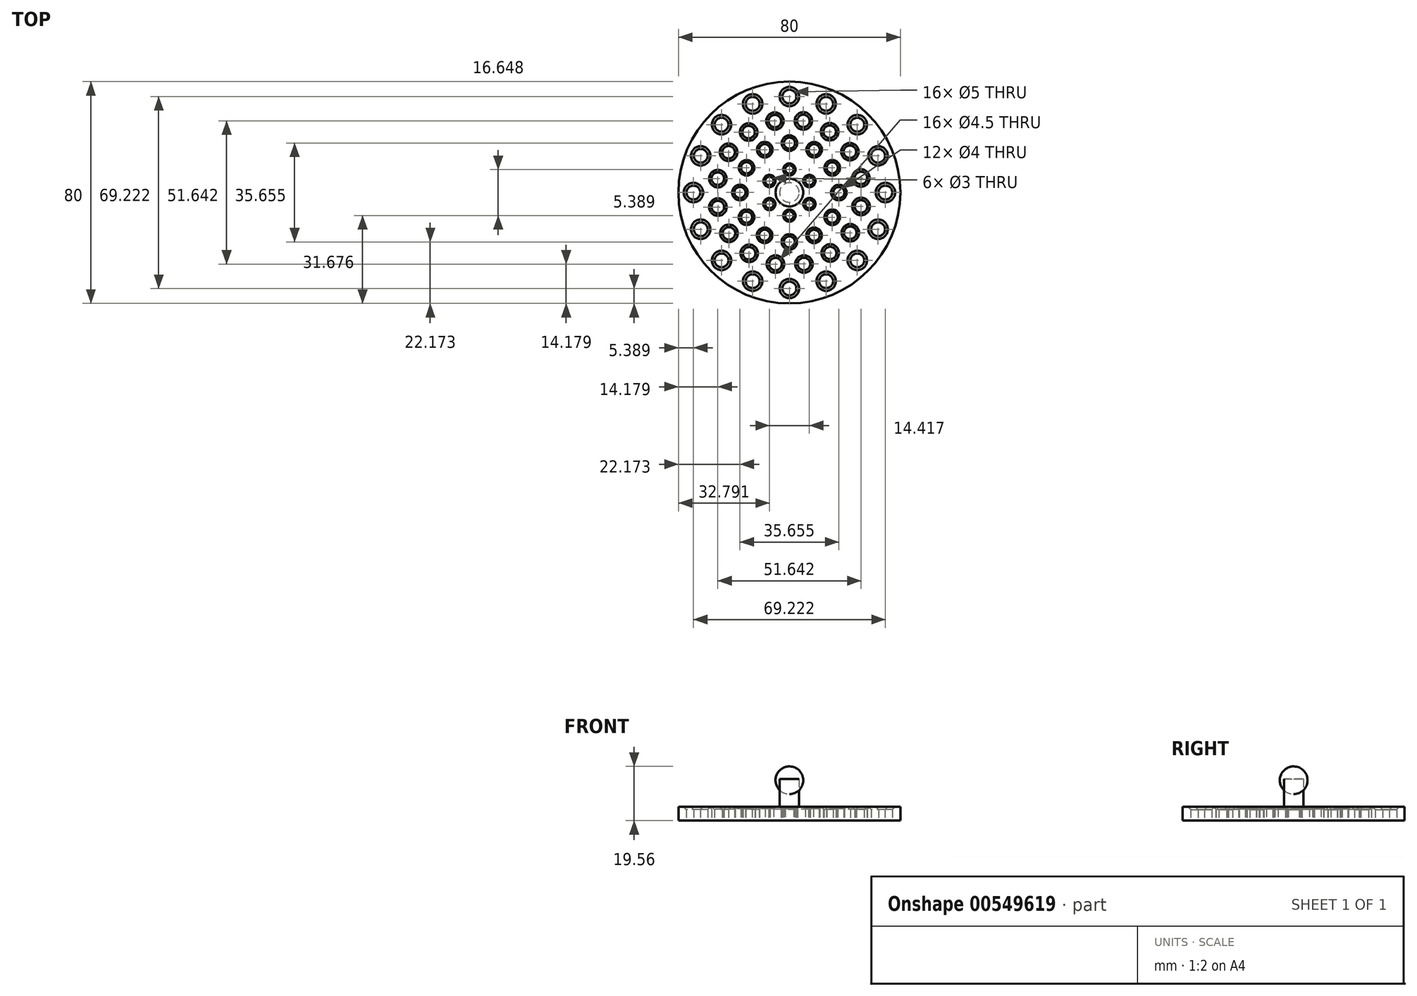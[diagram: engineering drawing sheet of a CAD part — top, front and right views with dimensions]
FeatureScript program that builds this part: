
annotation { "Feature Type Name" : "Feature", "Feature Type Description" : "" }
export const myFeature = defineFeature(function(context is Context, id is Id, definition is map)
    precondition{}
    {
        {
            var Q0;
            Q0=qCreatedBy(makeId("Top.planeOp"),FACE);
            var sketch = newSketch(context, id + "F0", { "sketchPlane" : qUnion([Q0])});
            skCircle(sketch, "E0", {"center": v(0, 0) * mm, "radius": 40 * mm});
            skCircle(sketch, "E1", {"center": v(0, 0) * mm, "radius": 3.5 * mm});
            skCircle(sketch, "E2", {"center": v(0, -34.61) * mm, "radius": 2.5 * mm});
            skCircle(sketch, "E3.1.0", {"center": v(13.25, -31.98) * mm, "radius": 2.5 * mm});
            skCircle(sketch, "E3.2.0", {"center": v(24.47, -24.47) * mm, "radius": 2.5 * mm});
            skCircle(sketch, "E4.1.3.0", {"center": v(31.98, -13.25) * mm, "radius": 2.5 * mm});
            skCircle(sketch, "E4.1.4.0", {"center": v(34.61, 0) * mm, "radius": 2.5 * mm});
            skCircle(sketch, "E4.1.5.0", {"center": v(31.98, 13.25) * mm, "radius": 2.5 * mm});
            skCircle(sketch, "E4.1.6.0", {"center": v(24.47, 24.47) * mm, "radius": 2.5 * mm});
            skCircle(sketch, "E4.1.7.0", {"center": v(13.25, 31.98) * mm, "radius": 2.5 * mm});
            skCircle(sketch, "E4.1.8.0", {"center": v(0, 34.61) * mm, "radius": 2.5 * mm});
            skCircle(sketch, "E4.1.9.0", {"center": v(-13.25, 31.98) * mm, "radius": 2.5 * mm});
            skCircle(sketch, "E5.1.10.0", {"center": v(-24.47, 24.47) * mm, "radius": 2.5 * mm});
            skCircle(sketch, "E5.1.11.0", {"center": v(-31.98, 13.25) * mm, "radius": 2.5 * mm});
            skCircle(sketch, "E6", {"center": v(-0.02, -17.83) * mm, "radius": 2 * mm});
            skCircle(sketch, "E7.1.0", {"center": v(8.9, -15.45) * mm, "radius": 2 * mm});
            skCircle(sketch, "E7.2.0", {"center": v(15.43, -8.93) * mm, "radius": 2 * mm});
            skCircle(sketch, "E8.1.3.0", {"center": v(17.83, -0.02) * mm, "radius": 2 * mm});
            skCircle(sketch, "E8.1.4.0", {"center": v(15.45, 8.9) * mm, "radius": 2 * mm});
            skCircle(sketch, "E8.1.5.0", {"center": v(8.93, 15.43) * mm, "radius": 2 * mm});
            skCircle(sketch, "E8.1.6.0", {"center": v(0.02, 17.83) * mm, "radius": 2 * mm});
            skCircle(sketch, "E8.1.7.0", {"center": v(-8.9, 15.45) * mm, "radius": 2 * mm});
            skCircle(sketch, "E9.1.8.0", {"center": v(-15.43, 8.93) * mm, "radius": 2 * mm});
            skCircle(sketch, "E9.1.9.0", {"center": v(-17.83, 0.02) * mm, "radius": 2 * mm});
            skCircle(sketch, "E10.1.12.0", {"center": v(-34.61, 0) * mm, "radius": 2.5 * mm});
            skCircle(sketch, "E10.1.13.0", {"center": v(-31.98, -13.25) * mm, "radius": 2.5 * mm});
            skCircle(sketch, "E11.1.10.0", {"center": v(-15.45, -8.9) * mm, "radius": 2 * mm});
            skCircle(sketch, "E11.1.11.0", {"center": v(-8.93, -15.43) * mm, "radius": 2 * mm});
            skCircle(sketch, "E12.1.14.0", {"center": v(-24.47, -24.47) * mm, "radius": 2.5 * mm});
            skCircle(sketch, "E12.1.15.0", {"center": v(-13.25, -31.98) * mm, "radius": 2.5 * mm});
            skCircle(sketch, "E13.2.0", {"center": v(-5.02, -25.82) * mm, "radius": 2.25 * mm});
            skCircle(sketch, "E14.1.0", {"center": v(5.24, -25.78) * mm, "radius": 2.25 * mm});
            skCircle(sketch, "E14.2.0", {"center": v(14.7, -21.8) * mm, "radius": 2.25 * mm});
            skCircle(sketch, "E14.3.0", {"center": v(21.93, -14.52) * mm, "radius": 2.25 * mm});
            skCircle(sketch, "E14.4.0", {"center": v(25.82, -5.02) * mm, "radius": 2.25 * mm});
            skCircle(sketch, "E14.5.0", {"center": v(25.78, 5.24) * mm, "radius": 2.25 * mm});
            skCircle(sketch, "E14.6.0", {"center": v(21.8, 14.7) * mm, "radius": 2.25 * mm});
            skCircle(sketch, "E14.7.0", {"center": v(14.52, 21.93) * mm, "radius": 2.25 * mm});
            skCircle(sketch, "E14.8.0", {"center": v(5.02, 25.82) * mm, "radius": 2.25 * mm});
            skCircle(sketch, "E14.9.0", {"center": v(-5.24, 25.78) * mm, "radius": 2.25 * mm});
            skCircle(sketch, "E14.10.0", {"center": v(-14.7, 21.8) * mm, "radius": 2.25 * mm});
            skCircle(sketch, "E14.11.0", {"center": v(-21.93, 14.52) * mm, "radius": 2.25 * mm});
            skCircle(sketch, "E14.12.0", {"center": v(-25.82, 5.02) * mm, "radius": 2.25 * mm});
            skCircle(sketch, "E14.13.0", {"center": v(-25.78, -5.24) * mm, "radius": 2.25 * mm});
            skCircle(sketch, "E14.14.0", {"center": v(-21.8, -14.7) * mm, "radius": 2.25 * mm});
            skCircle(sketch, "E14.15.0", {"center": v(-14.52, -21.93) * mm, "radius": 2.25 * mm});
            skCircle(sketch, "E15", {"center": v(0, -8.32) * mm, "radius": 1.5 * mm});
            skCircle(sketch, "E16.1.0", {"center": v(7.2, -4.16) * mm, "radius": 1.5 * mm});
            skCircle(sketch, "E16.2.0", {"center": v(7.2, 4.16) * mm, "radius": 1.5 * mm});
            skCircle(sketch, "E16.3.0", {"center": v(0, 8.32) * mm, "radius": 1.5 * mm});
            skCircle(sketch, "E17.1.4.0", {"center": v(-7.2, 4.16) * mm, "radius": 1.5 * mm});
            skCircle(sketch, "E17.1.5.0", {"center": v(-7.2, -4.16) * mm, "radius": 1.5 * mm});
            skSolve(sketch);
        }
        {
            var Q0;
            Q0=makeQuery(id+"F0.imprint","IMPRINT",FACE,{"disambiguationData":[TD([[makeQuery(id+"F0.imprint","IMPRINT",EDGE,{"derivedFrom":sQuery(id+"F0.wireOp",EDGE,"E0")}),1.0]])]});
            var Q1;
            Q1=sQuery(id+"F0.wireOp",EDGE,"E0");
            extrude(context, id + "F1", {"entities" : qUnion([Q0]), "surfaceEntities" : qUnion([Q1]), "depth" : 5 * mm, "offsetDistance" : 25 * mm});
        }
        {
            var Q0;
            Q0=makeQuery(id+"F0.imprint","IMPRINT",FACE,{"disambiguationData":[TD([[makeQuery(id+"F0.imprint","IMPRINT",EDGE,{"derivedFrom":sQuery(id+"F0.wireOp",EDGE,"E1")}),1.0]])]});
            var Q1;
            Q1=sQuery(id+"F0.wireOp",EDGE,"E1");
            extrude(context, id + "F2", {"entities" : qUnion([Q0]), "operationType" : NewBodyOperationType.ADD, "surfaceEntities" : qUnion([Q1]), "depth" : 15 * mm, "offsetDistance" : 25 * mm});
        }
        {
            var Q0;
            Q0=makeQuery(id+"F1.opExtrude","CAP_EDGE",EDGE,{"disambiguationData":[OSD([sQuery(id+"F0.wireOp",EDGE,"E10.1.12.0")])],"isStart":false});
            var Q1;
            Q1=makeQuery(id+"F1.opExtrude","CAP_EDGE",EDGE,{"disambiguationData":[OSD([sQuery(id+"F0.wireOp",EDGE,"E5.1.11.0")])],"isStart":false});
            var Q2;
            Q2=makeQuery(id+"F1.opExtrude","CAP_EDGE",EDGE,{"disambiguationData":[OSD([sQuery(id+"F0.wireOp",EDGE,"E5.1.10.0")])],"isStart":false});
            var Q3;
            Q3=makeQuery(id+"F1.opExtrude","CAP_EDGE",EDGE,{"disambiguationData":[OSD([sQuery(id+"F0.wireOp",EDGE,"E4.1.9.0")])],"isStart":false});
            var Q4;
            Q4=makeQuery(id+"F1.opExtrude","CAP_EDGE",EDGE,{"disambiguationData":[OSD([sQuery(id+"F0.wireOp",EDGE,"E4.1.8.0")])],"isStart":false});
            var Q5;
            Q5=makeQuery(id+"F1.opExtrude","CAP_EDGE",EDGE,{"disambiguationData":[OSD([sQuery(id+"F0.wireOp",EDGE,"E4.1.7.0")])],"isStart":false});
            var Q6;
            Q6=makeQuery(id+"F1.opExtrude","CAP_EDGE",EDGE,{"disambiguationData":[OSD([sQuery(id+"F0.wireOp",EDGE,"E4.1.6.0")])],"isStart":false});
            var Q7;
            Q7=makeQuery(id+"F1.opExtrude","CAP_EDGE",EDGE,{"disambiguationData":[OSD([sQuery(id+"F0.wireOp",EDGE,"E4.1.5.0")])],"isStart":false});
            var Q8;
            Q8=makeQuery(id+"F1.opExtrude","CAP_EDGE",EDGE,{"disambiguationData":[OSD([sQuery(id+"F0.wireOp",EDGE,"E4.1.4.0")])],"isStart":false});
            var Q9;
            Q9=makeQuery(id+"F1.opExtrude","CAP_EDGE",EDGE,{"disambiguationData":[OSD([sQuery(id+"F0.wireOp",EDGE,"E4.1.3.0")])],"isStart":false});
            var Q10;
            Q10=makeQuery(id+"F1.opExtrude","CAP_EDGE",EDGE,{"disambiguationData":[OSD([sQuery(id+"F0.wireOp",EDGE,"E3.2.0")])],"isStart":false});
            var Q11;
            Q11=makeQuery(id+"F1.opExtrude","CAP_EDGE",EDGE,{"disambiguationData":[OSD([sQuery(id+"F0.wireOp",EDGE,"E3.1.0")])],"isStart":false});
            var Q12;
            Q12=makeQuery(id+"F1.opExtrude","CAP_EDGE",EDGE,{"disambiguationData":[OSD([sQuery(id+"F0.wireOp",EDGE,"E2")])],"isStart":false});
            var Q13;
            Q13=makeQuery(id+"F1.opExtrude","CAP_EDGE",EDGE,{"disambiguationData":[OSD([sQuery(id+"F0.wireOp",EDGE,"E12.1.15.0")])],"isStart":false});
            var Q14;
            Q14=makeQuery(id+"F1.opExtrude","CAP_EDGE",EDGE,{"disambiguationData":[OSD([sQuery(id+"F0.wireOp",EDGE,"E12.1.14.0")])],"isStart":false});
            var Q15;
            Q15=makeQuery(id+"F1.opExtrude","CAP_EDGE",EDGE,{"disambiguationData":[OSD([sQuery(id+"F0.wireOp",EDGE,"E10.1.13.0")])],"isStart":false});
            chamfer(context, id + "F3", {"entities" : qUnion([Q0, Q1, Q2, Q3, Q4, Q5, Q6, Q7, Q8, Q9, Q10, Q11, Q12, Q13, Q14, Q15]), "width" : 1 * mm, "tangentPropagation" : true});
        }
        {
            var Q0;
            Q0=makeQuery(id+"F1.opExtrude","CAP_EDGE",EDGE,{"disambiguationData":[OSD([sQuery(id+"F0.wireOp",EDGE,"E14.11.0")])],"isStart":false});
            var Q1;
            Q1=makeQuery(id+"F1.opExtrude","CAP_EDGE",EDGE,{"disambiguationData":[OSD([sQuery(id+"F0.wireOp",EDGE,"E14.10.0")])],"isStart":false});
            var Q2;
            Q2=makeQuery(id+"F1.opExtrude","CAP_EDGE",EDGE,{"disambiguationData":[OSD([sQuery(id+"F0.wireOp",EDGE,"E14.8.0")])],"isStart":false});
            var Q3;
            Q3=makeQuery(id+"F1.opExtrude","CAP_EDGE",EDGE,{"disambiguationData":[OSD([sQuery(id+"F0.wireOp",EDGE,"E14.7.0")])],"isStart":false});
            var Q4;
            Q4=makeQuery(id+"F1.opExtrude","CAP_EDGE",EDGE,{"disambiguationData":[OSD([sQuery(id+"F0.wireOp",EDGE,"E14.6.0")])],"isStart":false});
            var Q5;
            Q5=makeQuery(id+"F1.opExtrude","CAP_EDGE",EDGE,{"disambiguationData":[OSD([sQuery(id+"F0.wireOp",EDGE,"E14.5.0")])],"isStart":false});
            var Q6;
            Q6=makeQuery(id+"F1.opExtrude","CAP_EDGE",EDGE,{"disambiguationData":[OSD([sQuery(id+"F0.wireOp",EDGE,"E14.4.0")])],"isStart":false});
            var Q7;
            Q7=makeQuery(id+"F1.opExtrude","CAP_EDGE",EDGE,{"disambiguationData":[OSD([sQuery(id+"F0.wireOp",EDGE,"E14.3.0")])],"isStart":false});
            var Q8;
            Q8=makeQuery(id+"F1.opExtrude","CAP_EDGE",EDGE,{"disambiguationData":[OSD([sQuery(id+"F0.wireOp",EDGE,"E14.2.0")])],"isStart":false});
            var Q9;
            Q9=makeQuery(id+"F1.opExtrude","CAP_EDGE",EDGE,{"disambiguationData":[OSD([sQuery(id+"F0.wireOp",EDGE,"E14.1.0")])],"isStart":false});
            var Q10;
            Q10=makeQuery(id+"F1.opExtrude","CAP_EDGE",EDGE,{"disambiguationData":[OSD([sQuery(id+"F0.wireOp",EDGE,"E13.2.0")])],"isStart":false});
            var Q11;
            Q11=makeQuery(id+"F1.opExtrude","CAP_EDGE",EDGE,{"disambiguationData":[OSD([sQuery(id+"F0.wireOp",EDGE,"E14.15.0")])],"isStart":false});
            var Q12;
            Q12=makeQuery(id+"F1.opExtrude","CAP_EDGE",EDGE,{"disambiguationData":[OSD([sQuery(id+"F0.wireOp",EDGE,"E14.14.0")])],"isStart":false});
            var Q13;
            Q13=makeQuery(id+"F1.opExtrude","CAP_EDGE",EDGE,{"disambiguationData":[OSD([sQuery(id+"F0.wireOp",EDGE,"E14.13.0")])],"isStart":false});
            var Q14;
            Q14=makeQuery(id+"F1.opExtrude","CAP_EDGE",EDGE,{"disambiguationData":[OSD([sQuery(id+"F0.wireOp",EDGE,"E14.12.0")])],"isStart":false});
            var Q15;
            Q15=makeQuery(id+"F1.opExtrude","CAP_EDGE",EDGE,{"disambiguationData":[OSD([sQuery(id+"F0.wireOp",EDGE,"E14.9.0")])],"isStart":false});
            chamfer(context, id + "F4", {"entities" : qUnion([Q0, Q1, Q2, Q3, Q4, Q5, Q6, Q7, Q8, Q9, Q10, Q11, Q12, Q13, Q14, Q15]), "width" : .9 * mm, "tangentPropagation" : true});
        }
        {
            var Q0;
            Q0=makeQuery(id+"F1.opExtrude","CAP_EDGE",EDGE,{"disambiguationData":[OSD([sQuery(id+"F0.wireOp",EDGE,"E9.1.8.0")])],"isStart":false});
            var Q1;
            Q1=makeQuery(id+"F1.opExtrude","CAP_EDGE",EDGE,{"disambiguationData":[OSD([sQuery(id+"F0.wireOp",EDGE,"E8.1.7.0")])],"isStart":false});
            var Q2;
            Q2=makeQuery(id+"F1.opExtrude","CAP_EDGE",EDGE,{"disambiguationData":[OSD([sQuery(id+"F0.wireOp",EDGE,"E8.1.6.0")])],"isStart":false});
            var Q3;
            Q3=makeQuery(id+"F1.opExtrude","CAP_EDGE",EDGE,{"disambiguationData":[OSD([sQuery(id+"F0.wireOp",EDGE,"E8.1.5.0")])],"isStart":false});
            var Q4;
            Q4=makeQuery(id+"F1.opExtrude","CAP_EDGE",EDGE,{"disambiguationData":[OSD([sQuery(id+"F0.wireOp",EDGE,"E8.1.4.0")])],"isStart":false});
            var Q5;
            Q5=makeQuery(id+"F1.opExtrude","CAP_EDGE",EDGE,{"disambiguationData":[OSD([sQuery(id+"F0.wireOp",EDGE,"E8.1.3.0")])],"isStart":false});
            var Q6;
            Q6=makeQuery(id+"F1.opExtrude","CAP_EDGE",EDGE,{"disambiguationData":[OSD([sQuery(id+"F0.wireOp",EDGE,"E7.2.0")])],"isStart":false});
            var Q7;
            Q7=makeQuery(id+"F1.opExtrude","CAP_EDGE",EDGE,{"disambiguationData":[OSD([sQuery(id+"F0.wireOp",EDGE,"E7.1.0")])],"isStart":false});
            var Q8;
            Q8=makeQuery(id+"F1.opExtrude","CAP_EDGE",EDGE,{"disambiguationData":[OSD([sQuery(id+"F0.wireOp",EDGE,"E6")])],"isStart":false});
            var Q9;
            Q9=makeQuery(id+"F1.opExtrude","CAP_EDGE",EDGE,{"disambiguationData":[OSD([sQuery(id+"F0.wireOp",EDGE,"E11.1.11.0")])],"isStart":false});
            var Q10;
            Q10=makeQuery(id+"F1.opExtrude","CAP_EDGE",EDGE,{"disambiguationData":[OSD([sQuery(id+"F0.wireOp",EDGE,"E11.1.10.0")])],"isStart":false});
            var Q11;
            Q11=makeQuery(id+"F1.opExtrude","CAP_EDGE",EDGE,{"disambiguationData":[OSD([sQuery(id+"F0.wireOp",EDGE,"E9.1.9.0")])],"isStart":false});
            chamfer(context, id + "F5", {"entities" : qUnion([Q0, Q1, Q2, Q3, Q4, Q5, Q6, Q7, Q8, Q9, Q10, Q11]), "width" : .8 * mm, "tangentPropagation" : true});
        }
        {
            var Q0;
            Q0=makeQuery(id+"F1.opExtrude","CAP_EDGE",EDGE,{"disambiguationData":[OSD([sQuery(id+"F0.wireOp",EDGE,"E16.3.0")])],"isStart":false});
            var Q1;
            Q1=makeQuery(id+"F1.opExtrude","CAP_EDGE",EDGE,{"disambiguationData":[OSD([sQuery(id+"F0.wireOp",EDGE,"E16.2.0")])],"isStart":false});
            var Q2;
            Q2=makeQuery(id+"F1.opExtrude","CAP_EDGE",EDGE,{"disambiguationData":[OSD([sQuery(id+"F0.wireOp",EDGE,"E16.1.0")])],"isStart":false});
            var Q3;
            Q3=makeQuery(id+"F1.opExtrude","CAP_EDGE",EDGE,{"disambiguationData":[OSD([sQuery(id+"F0.wireOp",EDGE,"E15")])],"isStart":false});
            var Q4;
            Q4=makeQuery(id+"F1.opExtrude","CAP_EDGE",EDGE,{"disambiguationData":[OSD([sQuery(id+"F0.wireOp",EDGE,"E17.1.5.0")])],"isStart":false});
            var Q5;
            Q5=makeQuery(id+"F1.opExtrude","CAP_EDGE",EDGE,{"disambiguationData":[OSD([sQuery(id+"F0.wireOp",EDGE,"E17.1.4.0")])],"isStart":false});
            chamfer(context, id + "F6", {"entities" : qUnion([Q0, Q1, Q2, Q3, Q4, Q5]), "width" : .7 * mm, "tangentPropagation" : true});
        }
        {
            var Q0;
            Q0=qCreatedBy(makeId("Front.planeOp"),FACE);
            var sketch = newSketch(context, id + "F7", { "sketchPlane" : qUnion([Q0])});
            skCircle(sketch, "E18", {"center": v(0, 14.56) * mm, "radius": 5 * mm});
            skLineSegment(sketch, "E19", {"start": v(0, 19.56) * mm, "end": v(0, 9.56) * mm});
            skSolve(sketch);
        }
        {
            var Q0;
            {var subQ0=sQuery(id+"F7.wireOp",EDGE,"E19");Q0=makeQuery(id+"F7.imprint","IMPRINT",FACE,{"disambiguationData":[TD([[makeQuery(id+"F7.imprint","IMPRINT",EDGE,{"derivedFrom":subQ0}),-1.0]])]});}
            var Q1;
            Q1=sQuery(id+"F7.wireOp",EDGE,"E18");
            var Q2;
            Q2=sQuery(id+"F7.wireOp",EDGE,"E19");
            revolve(context, id + "F8", {"entities" : qUnion([Q0]), "surfaceEntities" : qUnion([Q1]), "axis" : qUnion([Q2]), "revolveType" : RevolveType.FULL});
        }
    });
